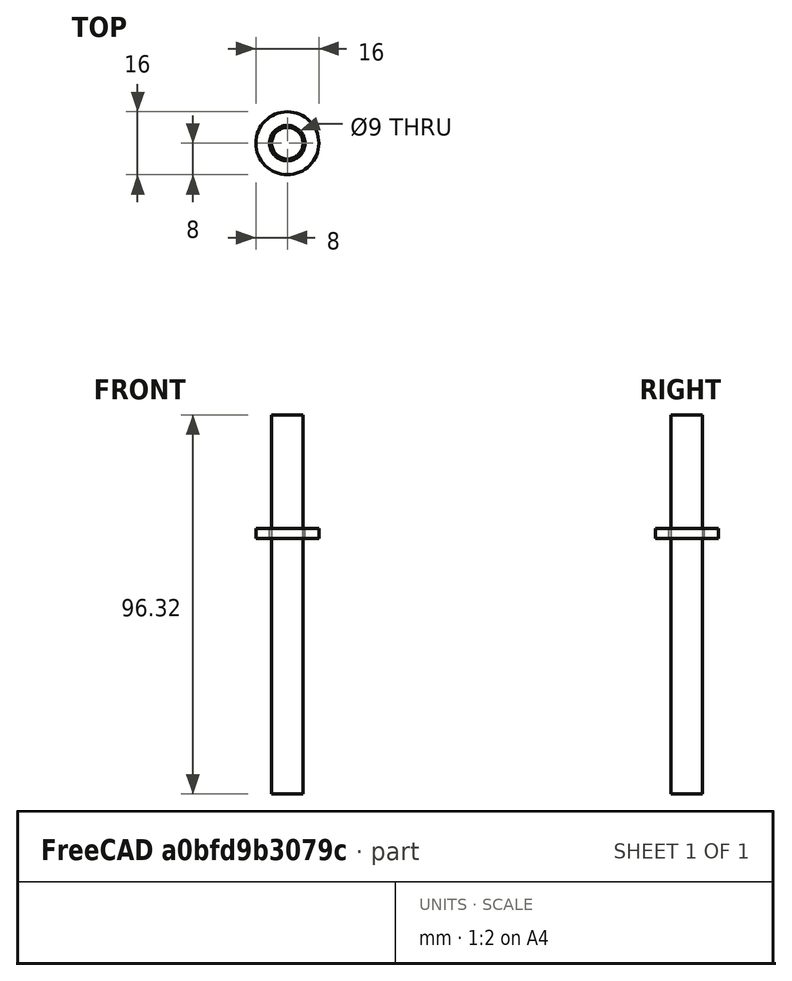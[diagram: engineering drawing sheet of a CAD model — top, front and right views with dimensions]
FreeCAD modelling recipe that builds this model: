
FCSTD DOCUMENT  (FreeCAD 1.0R39109 (Git))
Label: Studs_Hub_Base
License: All rights reserved
LicenseURL: http://en.wikipedia.org/wiki/All_rights_reserved
objects: App::Link×7, Part::FeaturePython×2, Spreadsheet::Sheet×1, Part::Cylinder×1, App::Part×1
note: 2 computed .brp shape members not serialized (recipe doc carries the construction recipe); baked Part::Feature solids carry a one-line shape summary decoded from their .brp
EXTERNAL_REF file=../../Master_of_Puppets.FCStd obj=Alternator
EXTERNAL_REF file=../../Master_of_Puppets.FCStd obj=Blade
EXTERNAL_REF file=../../Master_of_Puppets.FCStd obj=Fastener
EXTERNAL_REF file=../../Master_of_Puppets.FCStd obj=Hub
EXTERNAL_REF file=../../Master_of_Puppets.FCStd obj=Spreadsheet
EXTERNAL_REF file=../../Fasteners/Fastener_HexNut_HubHoles.FCStd obj=Binder
EXTERNAL_REF file=../../Fasteners/Fastener_Washer_Hub.FCStd obj=Tube
EXTERNAL_REF file=../../Fasteners/Fastener_Washer_Hub_Wide.FCStd obj=Tube

FEATURE [Spreadsheet::Sheet] Spreadsheet
  cells = A1='Inputs; A2='HubHolesRadius; B2(HubHolesRadius)==Master_of_Puppets#Hub.HubHolesRadius; A3='DistanceThreadsExtendFromNuts; B3(DistanceThreadsExtendFromNuts)==Master_of_Puppets#Fastener.DistanceThreadsExtendFromNuts; A4='HubHexNutThickness; B4(HubHexNutThickness)==Master_of_Puppets#Fastener.HubHexNutThickness; A5='WasherThickness; B5(WasherThickness)==Master_of_Puppets#Fastener.WasherThickness; A6='RotorDiskThickness; B6(RotorDiskThickness)==Master_of_Puppets#Spreadsheet.RotorDiskThickness; A7='MiddlePadThickness; B7(MiddlePadThickness)==Master_of_Puppets#Hub.MiddlePadThickness; A8='DistanceBetweenRotorDisks; B8(DistanceBetweenRotorDisks)==Master_of_Puppets#Alternator.DistanceBetweenRotorDisks; A9='NumberOfNutsBetweenRotorDisks; B9(NumberOfNutsBetweenRotorDisks)==Master_of_Puppets#Alternator.NumberOfNutsBetweenRotorDisks; A10='NumberOfWashersBetweenRotorDisks; B10(NumberOfWashersBetweenRotorDisks)==Master_of_Puppets#Alternator.NumberOfWashersBetweenRotorDisks; A11='BladeAssemblyPlateThickness; B11(BladeAssemblyPlateThickness)==Master_of_Puppets#Blade.BladeAssemblyPlateThickness; A12='BladeThickness; B12(BladeThickness)==Master_of_Puppets#Blade.BladeThickness; A13='HubStudsLength; B13(HubStudsLength)==Master_of_Puppets#Alternator.HubStudsLength; A14='FrontRotorCount; B14(FrontRotorCount)==Master_of_Puppets#Alternator.FrontRotorCount; A15='RotorTopology; B15(RotorTopology)==Master_of_Puppets#Spreadsheet.RotorTopology; A16='Calculated; A17='IsNonSingleRotorTopology; B17(IsNonSingleRotorTopology)==RotorTopology != <<Single>> ? 1 : 0; A18='BackFlangeHexNutZ; B18(BackFlangeHexNutZ)==HubStudsLength - HubHexNutThickness - (IsNonSingleRotorTopology == 1 ? DistanceThreadsExtendFromNuts : 0); A19='HexNutArrayZ; B19(HexNutArrayZ)==BackFlangeHexNutZ - HubHexNutThickness - RotorDiskThickness - MiddlePadThickness; A20='WasherArrayZ; B20(WasherArrayZ)==HexNutArrayZ - HubHexNutThickness * (NumberOfNutsBetweenRotorDisks - 1) - WasherThickness; A21='WasherArrayVisibility; B21(WasherArrayVisibility)==NumberOfWashersBetweenRotorDisks; A22='FrontDiskHexNut; B22(FrontDiskHexNut)==RotorTopology == <<Single>> ? HexNutArrayZ + HubHexNutThickness + WasherThickness : HexNutArrayZ - DistanceBetweenRotorDisks - RotorDiskThickness * FrontRotorCount; A23='WasherBladeAssemblyBackDisk; B23(WasherBladeAssemblyBackDisk)==FrontDiskHexNut - WasherThickness; A24='WasherBladeAssemblyFrontTriangle; B24(WasherBladeAssemblyFrontTriangle)==WasherBladeAssemblyBackDisk - BladeAssemblyPlateThickness - BladeThickness - BladeAssemblyPlateThickness - WasherThickness; A25='HexNutBladeAssemblyFrontTriangle; B25(HexNutBladeAssemblyFrontTriangle)==WasherBladeAssemblyFrontTriangle - HubHexNutThickness
FEATURE [Part::Cylinder] Cylinder  label="Thread"
  Angle = 360
  AttacherType = Attacher::AttachEngine3D
  FirstAngle = 0
  Height = 96.32
  Radius = 4
  SecondAngle = 0
  expr: Height = Spreadsheet.HubStudsLength
  expr: Radius = Spreadsheet.HubHolesRadius
FEATURE [App::Link] Link  label="HexNut_Flange_Back"
  LinkPlacement = pos=(0,0,89.41) rot=(0,0,1;0rad)
  LinkedObject = -> <external ../../Fasteners/Fastener_HexNut_HubHoles.FCStd>#Binder
  Placement = pos=(0,0,89.41) rot=(0,0,1;0rad)
  expr: .Placement.Base.z = Spreadsheet.BackFlangeHexNutZ
FEATURE [App::Link] Link001  label="HexNut_HubHoles"
  LinkedObject = -> <external ../../Fasteners/Fastener_HexNut_HubHoles.FCStd>#Binder
FEATURE [Part::FeaturePython] Array  label="HexNutArray"  # Draft array (typed FeaturePython)
  AlwaysSyncPlacement = false
  Angle = 360
  ArrayType = 0
  Axis = (0,0,1)
  Base = -> Link001
  Center = (0,0,0)
  Count = 1
  ExpandArray = false
  Fuse = false
  IntervalAxis = (0,0,0)
  IntervalX = (0,0,0)
  IntervalY = (0,0,0)
  IntervalZ = (0,0,-6.91)
  NumberCircles = 3
  NumberPolar = 5
  NumberX = 1
  NumberY = 1
  NumberZ = 0
  Placement = pos=(0,0,60.5) rot=(0,0,1;0rad)
  PlacementList = 1 placements: [(0,0,0)]
  RadialDistance = 50
  ScaleList = (1) [(1,1,1)]
  Symmetry = 1
  TangentialDistance = 25
  expr: .IntervalZ.z = -Spreadsheet.HubHexNutThickness
  expr: .Placement.Base.z = Spreadsheet.HexNutArrayZ
  expr: NumberZ = Spreadsheet.NumberOfNutsBetweenRotorDisks
  expr: Visibility = Spreadsheet.IsNonSingleRotorTopology
FEATURE [App::Link] Link002  label="Washer_Hub"
  LinkedObject = -> <external ../../Fasteners/Fastener_Washer_Hub.FCStd>#Tube
FEATURE [App::Link] Link003  label="HexNut_Rotor_Disk_Front"
  LinkPlacement = pos=(0,0,69.91) rot=(0,0,1;0rad)
  LinkedObject = -> <external ../../Fasteners/Fastener_HexNut_HubHoles.FCStd>#Binder
  Placement = pos=(0,0,69.91) rot=(0,0,1;0rad)
  expr: .Placement.Base.z = Spreadsheet.FrontDiskHexNut
  expr: Visibility = Spreadsheet.IsNonSingleRotorTopology
FEATURE [Part::FeaturePython] Array001  label="WasherArray"  # Draft array (typed FeaturePython)
  Angle = 360
  ArrayType = 0
  Axis = (0,0,1)
  Base = -> Link002
  Center = (0,0,0)
  Count = 1
  Fuse = false
  IntervalAxis = (0,0,0)
  IntervalX = (0,0,0)
  IntervalY = (0,0,0)
  IntervalZ = (0,0,-2.5)
  NumberCircles = 3
  NumberPolar = 5
  NumberX = 1
  NumberY = 1
  NumberZ = 0
  Placement = pos=(0,0,64.91) rot=(0,0,1;0rad)
  RadialDistance = 50
  Symmetry = 1
  TangentialDistance = 25
  expr: .IntervalZ.z = -Spreadsheet.WasherThickness
  expr: .Placement.Base.z = Spreadsheet.WasherArrayZ
  expr: NumberZ = Spreadsheet.NumberOfWashersBetweenRotorDisks
  expr: Visibility = Spreadsheet.WasherArrayVisibility
FEATURE [App::Link] Link004  label="Washer_BladeAssemblyBackDisk"
  LinkPlacement = pos=(0,0,67.41) rot=(0,0,1;0rad)
  LinkedObject = -> <external ../../Fasteners/Fastener_Washer_Hub_Wide.FCStd>#Tube
  Placement = pos=(0,0,67.41) rot=(0,0,1;0rad)
  expr: .Placement.Base.z = Spreadsheet.WasherBladeAssemblyBackDisk
  expr: Visibility = Spreadsheet.IsNonSingleRotorTopology
FEATURE [App::Link] Link005  label="Washer_BladeAssemblyFrontTriangle"
  LinkPlacement = pos=(0,0,11.91) rot=(0,0,1;0rad)
  LinkedObject = -> <external ../../Fasteners/Fastener_Washer_Hub_Wide.FCStd>#Tube
  Placement = pos=(0,0,11.91) rot=(0,0,1;0rad)
  expr: .Placement.Base.z = Spreadsheet.WasherBladeAssemblyFrontTriangle
FEATURE [App::Link] Link006  label="HexNut_BladeAssemblyFrontTriangle"
  LinkPlacement = pos=(0,0,5) rot=(0,0,1;0rad)
  LinkedObject = -> Link001
  Placement = pos=(0,0,5) rot=(0,0,1;0rad)
  expr: .Placement.Base.z = Spreadsheet.HexNutBladeAssemblyFrontTriangle
FEATURE [App::Part] Part  label="Studs_Hub_Base"
  Group = -> [Cylinder,Link,Link001,Array,Link003,Link002,Array001,Link004,Link005,Link006]
  Origin = -> Origin

RESOLVED EXTERNAL PARTS (link-assembly join: the EXTERNAL_REF files above that resolve inside this repo's crawl, each included once):
---- part ../../Fasteners/Fastener_HexNut_HubHoles.FCStd = doc fcstd_dba15245a95b ----
FCSTD DOCUMENT  (FreeCAD 0.21R33771 (Git))
Label: Fastener_HexNut_HubHoles
License: All rights reserved
LicenseURL: http://en.wikipedia.org/wiki/All_rights_reserved
objects: PartDesign::SubShapeBinder×1
note: 1 computed .brp shape members not serialized (recipe doc carries the construction recipe); baked Part::Feature solids carry a one-line shape summary decoded from their .brp
EXTERNAL_REF file=Fastener_HexNut.FCStd obj=Body

FEATURE [PartDesign::SubShapeBinder] Binder  label="Fastener_HexNut"
  BindCopyOnChange = 2
  BindMode = 0
  ClaimChildren = false
  Fuse = false
  MakeFace = true
  OffsetFill = false
  OffsetIntersection = false
  OffsetJoinType = 0
  OffsetOpenResult = false
  PartialLoad = false
  Relative = true
  Support = -> [<external Fastener_HexNut.FCStd>#Body]
  Variant = 1
  _Version = 2
---- part ../../Master_of_Puppets.FCStd = doc fcstd_6404554055c4 (61625 chars; too large to inline — full recipe in that document) ----
